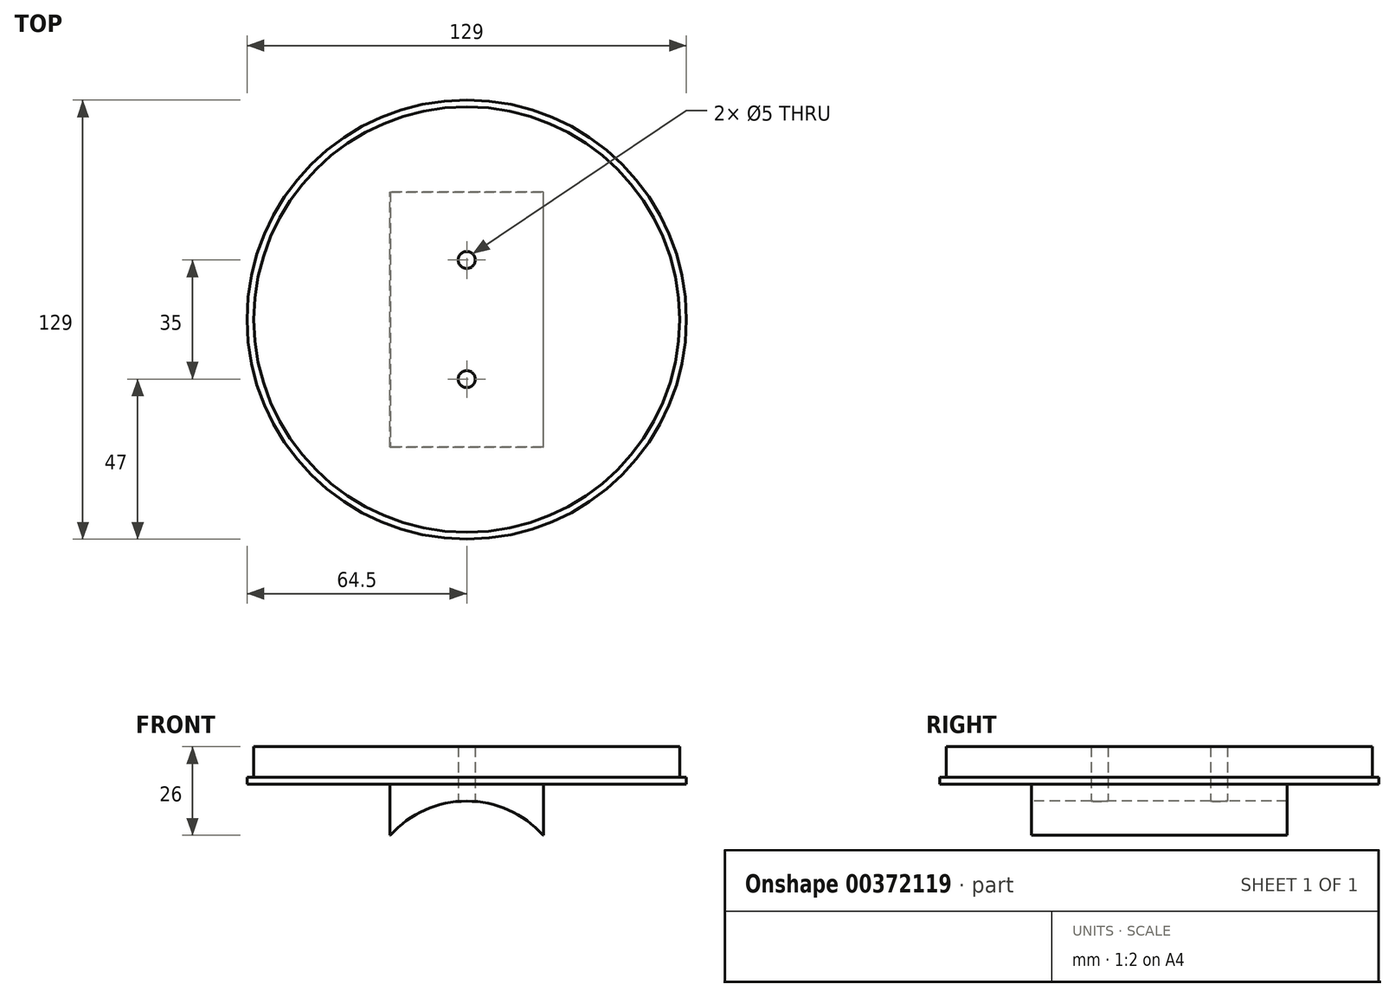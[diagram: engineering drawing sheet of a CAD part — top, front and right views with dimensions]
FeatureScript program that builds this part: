
annotation { "Feature Type Name" : "Feature", "Feature Type Description" : "" }
export const myFeature = defineFeature(function(context is Context, id is Id, definition is map)
    precondition{}
    {
        {
            var Q0;
            Q0=qCreatedBy(makeId("Top.planeOp"),FACE);
            var sketch = newSketch(context, id + "F0", { "sketchPlane" : qUnion([Q0])});
            skCircle(sketch, "E0", {"center": v(0, 0) * mm, "radius": 64.5 * mm});
            skSolve(sketch);
        }
        {
            var Q0;
            Q0 = qSketchRegion(id + "F0", true);
            extrude(context, id + "F1", {"entities" : qUnion([Q0]), "depth" : 2 * mm});
        }
        {
            var Q0;
            Q0=makeQuery(id+"F1.opExtrude","CAP_FACE",FACE,{"disambiguationData":[OSD([sQuery(id+"F0.wireOp",EDGE,"E0")])],"isStart":false});
            var sketch = newSketch(context, id + "F2", { "sketchPlane" : qUnion([Q0])});
            skCircle(sketch, "E1", {"center": v(0, 0) * mm, "radius": 62.5 * mm});
            skSolve(sketch);
        }
        {
            var Q0;
            Q0 = qSketchRegion(id + "F2", true);
            extrude(context, id + "F3", {"entities" : qUnion([Q0]), "operationType" : NewBodyOperationType.ADD, "depth" : 9 * mm});
        }
        {
            var Q0;
            Q0=makeQuery(id+"F1.opExtrude","CAP_FACE",FACE,{"disambiguationData":[OSD([sQuery(id+"F0.wireOp",EDGE,"E0")])],"isStart":true});
            var sketch = newSketch(context, id + "F4", { "sketchPlane" : qUnion([Q0])});
            skLineSegment(sketch, "E2.bottom", {"start": v(-22.5, 37.5) * mm, "end": v(22.5, 37.5) * mm});
            skLineSegment(sketch, "E2.top", {"start": v(-22.5, -37.5) * mm, "end": v(22.5, -37.5) * mm});
            skLineSegment(sketch, "E2.left", {"start": v(-22.5, 37.5) * mm, "end": v(-22.5, -37.5) * mm});
            skLineSegment(sketch, "E2.right", {"start": v(22.5, 37.5) * mm, "end": v(22.5, -37.5) * mm});
            skPoint(sketch, "E2.middle", {"position": v(0, 0) * mm});
            skSolve(sketch);
        }
        {
            var Q0;
            Q0 = qSketchRegion(id + "F4", true);
            extrude(context, id + "F5", {"entities" : qUnion([Q0]), "operationType" : NewBodyOperationType.ADD, "depth" : 15 * mm});
        }
        {
            var Q0;
            Q0=makeQuery(id+"F5.opExtrude","CAP_FACE",FACE,{"disambiguationData":[OSD([sQuery(id+"F4.wireOp",EDGE,"E2.bottom"),sQuery(id+"F4.wireOp",EDGE,"E2.top"),sQuery(id+"F4.wireOp",EDGE,"E2.left"),sQuery(id+"F4.wireOp",EDGE,"E2.right")])],"isStart":false});
            var sketch = newSketch(context, id + "F6", { "sketchPlane" : qUnion([Q0])});
            skLineSegment(sketch, "E3.0", {"start": v(-17.5, 32.5) * mm, "end": v(-17.5, -32.5) * mm});
            skLineSegment(sketch, "E3.1", {"start": v(17.5, 32.5) * mm, "end": v(-17.5, 32.5) * mm});
            skLineSegment(sketch, "E3.2", {"start": v(17.5, -32.5) * mm, "end": v(17.5, 32.5) * mm});
            skLineSegment(sketch, "E3.3", {"start": v(-17.5, -32.5) * mm, "end": v(17.5, -32.5) * mm});
            skSolve(sketch);
        }
        {
            var Q0;
            Q0=makeQuery(id+"F5.opExtrude","SWEPT_FACE",FACE,{"disambiguationData":[OSD([sQuery(id+"F4.wireOp",EDGE,"E2.bottom")])]});
            var sketch = newSketch(context, id + "F7", { "sketchPlane" : qUnion([Q0])});
            skLineSegment(sketch, "E4", {"start": v(0, 0) * mm, "end": v(0, -35) * mm, "construction": true});
            skPoint(sketch, "E4.endSnap0", {"position": v(0, -15) * mm});
            skCircle(sketch, "E5", {"center": v(0, -35) * mm, "radius": 30 * mm});
            skSolve(sketch);
        }
        {
            var Q0;
            {var subQ0=sQuery(id+"F7.wireOp",EDGE,"E5");var subQ1=makeQuery(id+"F5.opExtrude","CAP_EDGE",EDGE,{"disambiguationData":[OSD([sQuery(id+"F4.wireOp",EDGE,"E2.bottom")])],"isStart":false});var subQ2=makeQuery(id+"F7.imprint","INTERSECT",VERTEX,{"disambiguationData":[OD(0.0)],"derivedFrom":[subQ1,subQ0]});Q0=makeQuery(id+"F7.imprint","IMPRINT",FACE,{"disambiguationData":[TD([[makeQuery(id+"F7.imprint","IMPRINT",EDGE,{"disambiguationData":[TD([[subQ2,1.0]])],"derivedFrom":subQ0}),1.0]])]});}
            extrude(context, id + "F8", {"entities" : qUnion([Q0]), "operationType" : NewBodyOperationType.REMOVE, "oppositeDirection" : true, "depth" : 75 * mm});
        }
        {
            var Q0;
            Q0=makeQuery(id+"F6.imprint","IMPRINT",FACE,{"disambiguationData":[TD([[makeQuery(id+"F6.imprint","IMPRINT",EDGE,{"derivedFrom":sQuery(id+"F6.wireOp",EDGE,"E3.0")}),1.0]])]});
            var sketch = newSketch(context, id + "F9", { "sketchPlane" : qUnion([Q0])});
            skLineSegment(sketch, "E6", {"start": v(0, 32.5) * mm, "end": v(0, 17.5) * mm, "construction": true});
            skPoint(sketch, "E6.endSnap0", {"position": v(0, 32.5) * mm});
            skLineSegment(sketch, "E7", {"start": v(0, -32.5) * mm, "end": v(0, -17.5) * mm, "construction": true});
            skPoint(sketch, "E7.endSnap0", {"position": v(0, -32.5) * mm});
            skLineSegment(sketch, "E8", {"start": v(0, -17.5) * mm, "end": v(0, -2.5) * mm, "construction": true});
            skLineSegment(sketch, "E9", {"start": v(0, 17.5) * mm, "end": v(0, 2.5) * mm, "construction": true});
            skCircle(sketch, "E10", {"center": v(0, 17.5) * mm, "radius": 2.5 * mm});
            skCircle(sketch, "E11", {"center": v(0, -17.5) * mm, "radius": 2.5 * mm});
            skSolve(sketch);
        }
        {
            var Q0;
            Q0 = qSketchRegion(id + "F9", true);
            extrude(context, id + "F10", {"entities" : qUnion([Q0]), "operationType" : NewBodyOperationType.REMOVE, "oppositeDirection" : true, "depth" : 35 * mm});
        }
    });
